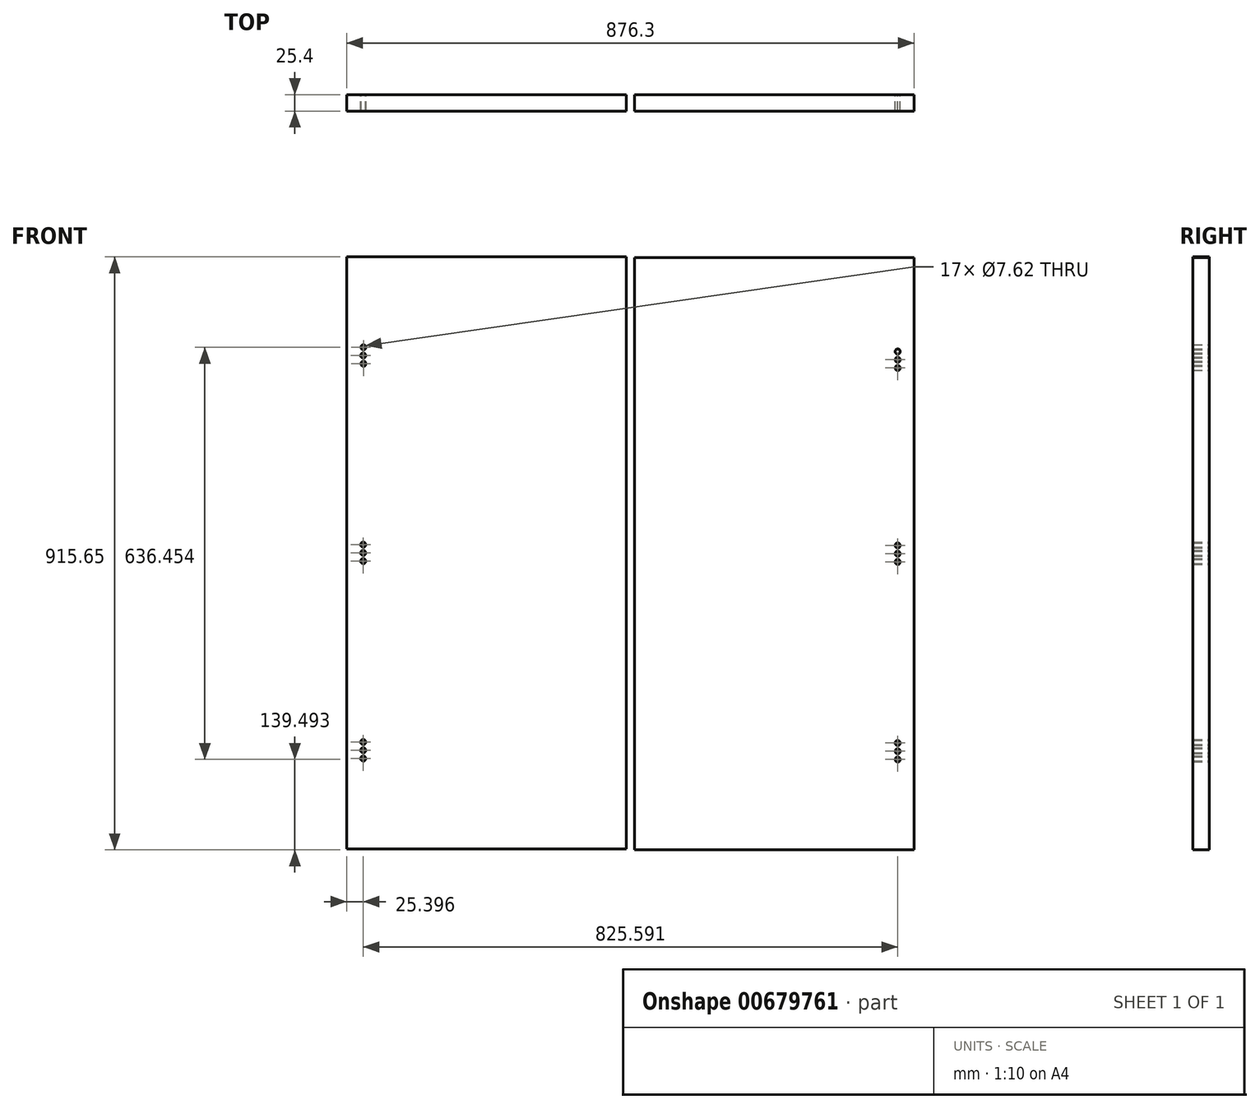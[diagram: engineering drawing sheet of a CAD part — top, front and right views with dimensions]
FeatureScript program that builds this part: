
annotation { "Feature Type Name" : "Feature", "Feature Type Description" : "" }
export const myFeature = defineFeature(function(context is Context, id is Id, definition is map)
    precondition{}
    {
        {
            var Q0;
            Q0=qCreatedBy(makeId("Front.planeOp"),FACE);
            var sketch = newSketch(context, id + "F0", { "sketchPlane" : qUnion([Q0])});
            skLineSegment(sketch, "E0.bottom", {"start": v(-153.67, -623.97) * mm, "end": v(-585.47, -623.97) * mm});
            skLineSegment(sketch, "E0.top", {"start": v(-153.67, 290.43) * mm, "end": v(-585.47, 290.43) * mm});
            skLineSegment(sketch, "E0.left", {"start": v(-153.67, -623.97) * mm, "end": v(-153.67, 290.43) * mm});
            skLineSegment(sketch, "E0.right", {"start": v(-585.47, -623.97) * mm, "end": v(-585.47, 290.43) * mm});
            skPoint(sketch, "E0.middle", {"position": v(-369.57, -166.77) * mm});
            skLineSegment(sketch, "E1.bottom", {"start": v(290.83, -625.22) * mm, "end": v(-140.97, -625.22) * mm});
            skLineSegment(sketch, "E1.top", {"start": v(290.83, 289.18) * mm, "end": v(-140.97, 289.18) * mm});
            skLineSegment(sketch, "E1.left", {"start": v(290.83, -625.22) * mm, "end": v(290.83, 289.18) * mm});
            skLineSegment(sketch, "E1.right", {"start": v(-140.97, -625.22) * mm, "end": v(-140.97, 289.18) * mm});
            skPoint(sketch, "E1.middle", {"position": v(74.93, -168.02) * mm});
            skPoint(sketch, "E2", {"position": v(-559.7, 150.73) * mm});
            skPoint(sketch, "E3", {"position": v(-560.07, 138.03) * mm});
            skPoint(sketch, "E4", {"position": v(-559.61, 125.33) * mm});
            skLineSegment(sketch, "E5", {"start": v(-369.57, -166.77) * mm, "end": v(-680, -166.77) * mm});
            skLineSegment(sketch, "E6", {"start": v(-351.7, 138.03) * mm, "end": v(-677.58, 138.03) * mm});
            skPoint(sketch, "E7", {"position": v(-560.07, -166.77) * mm});
            skPoint(sketch, "E8", {"position": v(-560.07, -154.07) * mm});
            skPoint(sketch, "E9", {"position": v(-560.07, -179.47) * mm});
            skPoint(sketch, "E10", {"position": v(-560.07, -458.87) * mm});
            skPoint(sketch, "E11", {"position": v(-560.07, -484.27) * mm});
            skPoint(sketch, "E12", {"position": v(-560.07, -471.57) * mm});
            skLineSegment(sketch, "E13", {"start": v(-422.02, -471.57) * mm, "end": v(-678.27, -471.57) * mm});
            skLineSegment(sketch, "E14", {"start": v(-560.07, -442.13) * mm, "end": v(-560.07, -493.63) * mm});
            skPoint(sketch, "E15", {"position": v(265.43, 144.19) * mm});
            skPoint(sketch, "E16", {"position": v(265.52, 144.19) * mm});
            skPoint(sketch, "E17", {"position": v(265.52, 131.49) * mm});
            skPoint(sketch, "E18", {"position": v(265.43, -155.32) * mm});
            skPoint(sketch, "E19", {"position": v(265.43, -168.02) * mm});
            skPoint(sketch, "E20", {"position": v(265.43, -180.72) * mm});
            skPoint(sketch, "E21", {"position": v(265.43, -460.33) * mm});
            skPoint(sketch, "E22", {"position": v(265.5, -473.03) * mm});
            skPoint(sketch, "E23", {"position": v(265.5, -485.73) * mm});
            skLineSegment(sketch, "E24", {"start": v(513.95, -168.02) * mm, "end": v(620.7, -168.02) * mm});
            skLineSegment(sketch, "E25", {"start": v(528.2, -473.18) * mm, "end": v(599.37, -473.18) * mm});
            skLineSegment(sketch, "E26", {"start": v(265.52, 163.44) * mm, "end": v(265.52, 104.54) * mm});
            skLineSegment(sketch, "E27", {"start": v(549.58, -142.96) * mm, "end": v(549.58, -200.82) * mm});
            skLineSegment(sketch, "E28", {"start": v(265.5, -444.82) * mm, "end": v(265.5, -501.23) * mm});
            skLineSegment(sketch, "E29", {"start": v(-559.61, 162.25) * mm, "end": v(-560.07, 100.43) * mm});
            skLineSegment(sketch, "E30", {"start": v(-559.77, -130.57) * mm, "end": v(-559.77, -201.81) * mm});
            skPoint(sketch, "E31", {"position": v(265.52, 118.79) * mm});
            skSolve(sketch);
        }
        {
            var Q0;
            {var subQ1=sQuery(id+"F0.wireOp",EDGE,"E0.bottom");Q0=makeQuery(id+"F0.imprint","IMPRINT",FACE,{"disambiguationData":[TD([[makeQuery(id+"F0.imprint","IMPRINT",EDGE,{"derivedFrom":subQ1}),-1.0]])]});}
            var Q1;
            {var subQ3=sQuery(id+"F0.wireOp",EDGE,"E1.bottom");Q1=makeQuery(id+"F0.imprint","IMPRINT",FACE,{"disambiguationData":[TD([[makeQuery(id+"F0.imprint","IMPRINT",EDGE,{"derivedFrom":subQ3}),-1.0]])]});}
            extrude(context, id + "F1", {"entities" : qUnion([Q0, Q1]), "depth" : 25.4 * mm, "offsetDistance" : 25.4 * mm});
        }
        {
            var Q0;
            Q0=sQuery(id+"F0.wireOp",VERTEX,"E2");
            var Q1;
            Q1=sQuery(id+"F0.wireOp",VERTEX,"E3");
            var Q2;
            Q2=sQuery(id+"F0.wireOp",VERTEX,"E4");
            var Q3;
            Q3=sQuery(id+"F0.wireOp",VERTEX,"E8");
            var Q4;
            Q4=sQuery(id+"F0.wireOp",VERTEX,"E7");
            var Q5;
            Q5=sQuery(id+"F0.wireOp",VERTEX,"E9");
            var Q6;
            Q6=sQuery(id+"F0.wireOp",VERTEX,"E10");
            var Q7;
            Q7=sQuery(id+"F0.wireOp",VERTEX,"E11");
            var Q8;
            Q8=sQuery(id+"F0.wireOp",VERTEX,"E12");
            var Q9;
            Q9=sQuery(id+"F0.wireOp",VERTEX,"E23");
            var Q10;
            Q10=sQuery(id+"F0.wireOp",VERTEX,"E22");
            var Q11;
            Q11=sQuery(id+"F0.wireOp",VERTEX,"E21");
            var Q12;
            Q12=sQuery(id+"F0.wireOp",VERTEX,"E20");
            var Q13;
            Q13=sQuery(id+"F0.wireOp",VERTEX,"E19");
            var Q14;
            Q14=sQuery(id+"F0.wireOp",VERTEX,"E18");
            var Q15;
            Q15=sQuery(id+"F0.wireOp",VERTEX,"E17");
            var Q16;
            Q16=sQuery(id+"F0.wireOp",VERTEX,"E15");
            var Q17;
            Q17=sQuery(id+"F0.wireOp",VERTEX,"E16");
            var Q18;
            Q18=sQuery(id+"F0.wireOp",VERTEX,"E31");
            var Q19;
            Q19=makeQuery(id+"F1.opExtrude","SWEPT_BODY",BODY,{"disambiguationData":[OSD([sQuery(id+"F0.wireOp",EDGE,"E0.bottom"),sQuery(id+"F0.wireOp",EDGE,"E0.top"),sQuery(id+"F0.wireOp",EDGE,"E0.left"),sQuery(id+"F0.wireOp",EDGE,"E0.right")])]});
            var Q20;
            Q20=makeQuery(id+"F1.opExtrude","SWEPT_BODY",BODY,{"disambiguationData":[OSD([sQuery(id+"F0.wireOp",EDGE,"E1.bottom"),sQuery(id+"F0.wireOp",EDGE,"E1.top"),sQuery(id+"F0.wireOp",EDGE,"E1.left"),sQuery(id+"F0.wireOp",EDGE,"E1.right")])]});
            hole(context, id + "F2", {"style" : HoleStyle.C_SINK, "endStyle" : HoleEndStyle.THROUGH, "oppositeDirection" : true, "holeDiameter" : 7.62 * mm, "cSinkDiameter" : 9.52 * mm, "cSinkAngle" : 90 * degree, "majorDiameter" : 6.35 * mm, "isTappedThrough" : true, "tappedDepth" : 12.7 * mm, "tapClearance" : 3, "locations" : qUnion([Q0, Q1, Q2, Q3, Q4, Q5, Q6, Q7, Q8, Q9, Q10, Q11, Q12, Q13, Q14, Q15, Q16, Q17, Q18]), "scope" : qUnion([Q19, Q20])});
        }
    });
